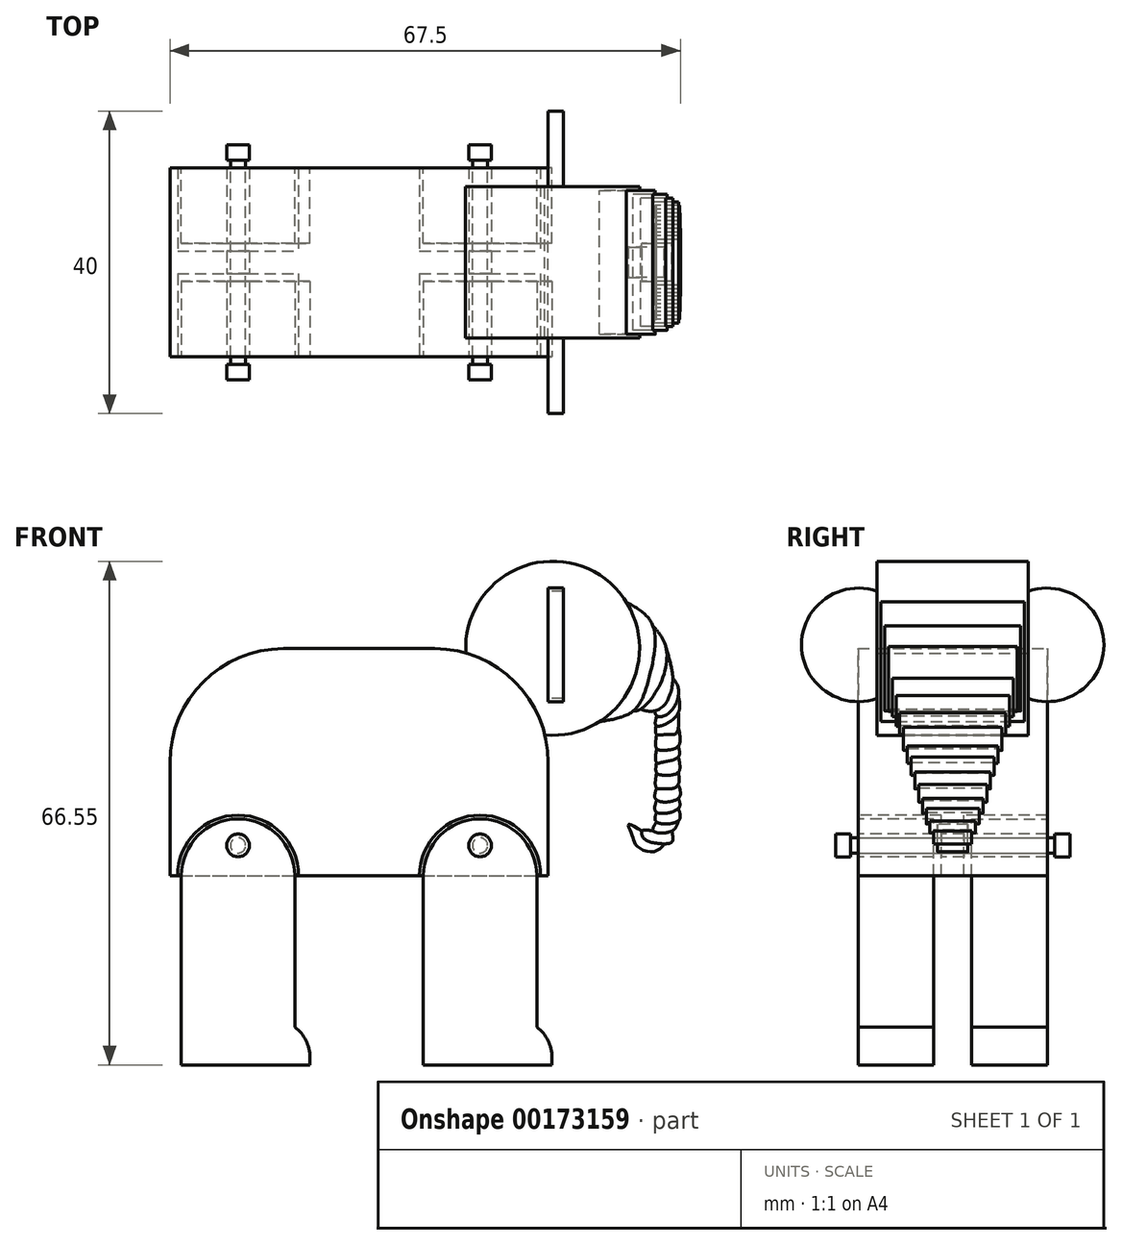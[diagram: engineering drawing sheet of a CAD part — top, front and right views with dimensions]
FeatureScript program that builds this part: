
annotation { "Feature Type Name" : "Feature", "Feature Type Description" : "" }
export const myFeature = defineFeature(function(context is Context, id is Id, definition is map)
    precondition{}
    {
        {
            var Q0;
            Q0=qCreatedBy(makeId("Front.planeOp"),FACE);
            var sketch = newSketch(context, id + "F0", { "sketchPlane" : qUnion([Q0])});
            skLineSegment(sketch, "E0.bottom", {"start": v(0, 0) * mm, "end": v(25, 0) * mm});
            skLineSegment(sketch, "E0.top", {"start": v(0, 30) * mm, "end": v(25, 30) * mm});
            skLineSegment(sketch, "E0.left", {"start": v(0, 0) * mm, "end": v(0, 30) * mm});
            skLineSegment(sketch, "E0.right", {"start": v(25, 0) * mm, "end": v(25, 30) * mm});
            skLineSegment(sketch, "E1.bottom", {"start": v(0, 0) * mm, "end": v(-25, 0) * mm});
            skLineSegment(sketch, "E1.top", {"start": v(0, 30) * mm, "end": v(-25, 30) * mm});
            skLineSegment(sketch, "E1.right", {"start": v(-25, 0) * mm, "end": v(-25, 30) * mm});
            skSolve(sketch);
        }
        {
            var Q0;
            Q0=makeQuery(id+"F0.imprint","IMPRINT",FACE,{"disambiguationData":[TD([[makeQuery(id+"F0.imprint","IMPRINT",EDGE,{"derivedFrom":sQuery(id+"F0.wireOp",EDGE,"E1.bottom")}),-1.0]])]});
            var Q1;
            Q1=makeQuery(id+"F0.imprint","IMPRINT",FACE,{"disambiguationData":[TD([[makeQuery(id+"F0.imprint","IMPRINT",EDGE,{"derivedFrom":sQuery(id+"F0.wireOp",EDGE,"E0.bottom")}),1.0]])]});
            extrude(context, id + "F1", {"entities" : qUnion([Q0, Q1]), "endBound" : BoundingType.SYMMETRIC, "depth" : 25 * mm});
        }
        {
            var Q0;
            Q0=makeQuery(id+"F1.opExtrude","SWEPT_EDGE",EDGE,{"disambiguationData":[OSD([sQuery(id+"F0.wireOp",EDGE,"E0.top"),sQuery(id+"F0.wireOp",EDGE,"E0.right")])]});
            var Q1;
            Q1=makeQuery(id+"F1.opExtrude","SWEPT_EDGE",EDGE,{"disambiguationData":[OSD([sQuery(id+"F0.wireOp",EDGE,"E1.top"),sQuery(id+"F0.wireOp",EDGE,"E1.right")])]});
            fillet(context, id + "F2", {"entities" : qUnion([Q0, Q1]), "radius" : 15 * mm, "tangentPropagation" : true, "allowEdgeOverflow" : false});
        }
        {
            var Q0;
            Q0=makeQuery(id+"F1.opExtrude","CAP_FACE",FACE,{"disambiguationData":[OSD([sQuery(id+"F0.wireOp",EDGE,"E0.bottom"),sQuery(id+"F0.wireOp",EDGE,"E0.top"),sQuery(id+"F0.wireOp",EDGE,"E0.right"),sQuery(id+"F0.wireOp",EDGE,"E1.bottom"),sQuery(id+"F0.wireOp",EDGE,"E1.top"),sQuery(id+"F0.wireOp",EDGE,"E1.right")])],"isStart":false});
            var sketch = newSketch(context, id + "F3", { "sketchPlane" : qUnion([Q0])});
            skCircle(sketch, "E2", {"center": v(-16, 0) * mm, "radius": 8 * mm});
            skCircle(sketch, "E3", {"center": v(16, 0) * mm, "radius": 8 * mm});
            skSolve(sketch);
        }
        {
            var Q0;
            Q0=sQuery(id+"F3.wireOp",VERTEX,"E2.center");
            var Q1;
            Q1=sQuery(id+"F3.wireOp",VERTEX,"E3.center");
            var Q2;
            Q2=makeQuery(id+"F1.opExtrude","SWEPT_BODY",BODY,{"disambiguationData":[OSD([sQuery(id+"F0.wireOp",EDGE,"E0.bottom"),sQuery(id+"F0.wireOp",EDGE,"E0.top"),sQuery(id+"F0.wireOp",EDGE,"E0.right"),sQuery(id+"F0.wireOp",EDGE,"E1.bottom"),sQuery(id+"F0.wireOp",EDGE,"E1.top"),sQuery(id+"F0.wireOp",EDGE,"E1.right")])]});
            hole(context, id + "F4", {"style" : HoleStyle.SIMPLE, "endStyle" : HoleEndStyle.THROUGH, "holeDiameter" : 16 * mm, "startFromSketch" : true, "locations" : qUnion([Q0, Q1]), "scope" : qUnion([Q2]), "isTappedThrough" : true});
        }
        {
            var Q0;
            Q0=qCreatedBy(makeId("Top.planeOp"),FACE);
            var sketch = newSketch(context, id + "F5", { "sketchPlane" : qUnion([Q0])});
            skLineSegment(sketch, "E4.bottom", {"start": v(-25, -1.5) * mm, "end": v(25, -1.5) * mm});
            skLineSegment(sketch, "E4.top", {"start": v(-25, 1.5) * mm, "end": v(25, 1.5) * mm});
            skLineSegment(sketch, "E4.left", {"start": v(-25, -1.5) * mm, "end": v(-25, 1.5) * mm});
            skLineSegment(sketch, "E4.right", {"start": v(25, -1.5) * mm, "end": v(25, 1.5) * mm});
            skSolve(sketch);
        }
        {
            var Q0;
            Q0=makeQuery(id+"F5.imprint","IMPRINT",FACE,{"disambiguationData":[TD([[makeQuery(id+"F5.imprint","IMPRINT",EDGE,{"derivedFrom":sQuery(id+"F5.wireOp",EDGE,"E4.bottom")}),1.0]])]});
            var Q1;
            Q1=makeQuery(id+"F1.opExtrude","SWEPT_BODY",BODY,{"disambiguationData":[OSD([sQuery(id+"F0.wireOp",EDGE,"E0.bottom"),sQuery(id+"F0.wireOp",EDGE,"E0.top"),sQuery(id+"F0.wireOp",EDGE,"E0.right"),sQuery(id+"F0.wireOp",EDGE,"E1.bottom"),sQuery(id+"F0.wireOp",EDGE,"E1.top"),sQuery(id+"F0.wireOp",EDGE,"E1.right")])]});
            extrude(context, id + "F6", {"entities" : qUnion([Q0]), "operationType" : NewBodyOperationType.ADD, "endBound" : BoundingType.UP_TO_BODY, "endBoundEntityBody" : qUnion([Q1]), "depth" : 25 * mm});
        }
        {
            var Q0;
            Q0=makeQuery(id+"F1.opExtrude","CAP_FACE",FACE,{"disambiguationData":[OSD([sQuery(id+"F0.wireOp",EDGE,"E0.bottom"),sQuery(id+"F0.wireOp",EDGE,"E0.top"),sQuery(id+"F0.wireOp",EDGE,"E0.right"),sQuery(id+"F0.wireOp",EDGE,"E1.bottom"),sQuery(id+"F0.wireOp",EDGE,"E1.top"),sQuery(id+"F0.wireOp",EDGE,"E1.right")])],"isStart":false});
            var sketch = newSketch(context, id + "F7", { "sketchPlane" : qUnion([Q0])});
            skLineSegment(sketch, "E5.top", {"start": v(-23.5, -25) * mm, "end": v(-8.5, -25) * mm});
            skLineSegment(sketch, "E5.left", {"start": v(-23.5, 0) * mm, "end": v(-23.5, -25) * mm});
            skLineSegment(sketch, "E5.right", {"start": v(-8.5, 0) * mm, "end": v(-8.5, -25) * mm});
            skArc(sketch, "E6", {"start": v(-8.5, 0) * mm, "mid": v(-16, 7.5) * mm, "end": v(-23.5, 0) * mm});
            skLineSegment(sketch, "E7", {"start": v(-23.5, 0) * mm, "end": v(-8.5, 0) * mm});
            skLineSegment(sketch, "E8.bottom", {"start": v(8.5, 0) * mm, "end": v(23.5, 0) * mm});
            skLineSegment(sketch, "E8.top", {"start": v(8.5, -25) * mm, "end": v(23.5, -25) * mm});
            skLineSegment(sketch, "E8.left", {"start": v(8.5, 0) * mm, "end": v(8.5, -25) * mm});
            skLineSegment(sketch, "E8.right", {"start": v(23.5, 0) * mm, "end": v(23.5, -25) * mm});
            skCircle(sketch, "E9", {"center": v(16, 0) * mm, "radius": 7.5 * mm});
            skLineSegment(sketch, "E10.bottom", {"start": v(-8.5, -25) * mm, "end": v(-6.5, -25) * mm});
            skLineSegment(sketch, "E10.top", {"start": v(-8.5, -20) * mm, "end": v(-6.5, -20) * mm});
            skLineSegment(sketch, "E10.left", {"start": v(-8.5, -25) * mm, "end": v(-8.5, -20) * mm});
            skLineSegment(sketch, "E10.right", {"start": v(-6.5, -25) * mm, "end": v(-6.5, -20) * mm});
            skLineSegment(sketch, "E11.bottom", {"start": v(23.5, -25) * mm, "end": v(25.5, -25) * mm});
            skLineSegment(sketch, "E11.top", {"start": v(23.5, -20) * mm, "end": v(25.5, -20) * mm});
            skLineSegment(sketch, "E11.left", {"start": v(23.5, -25) * mm, "end": v(23.5, -20) * mm});
            skLineSegment(sketch, "E11.right", {"start": v(25.5, -25) * mm, "end": v(25.5, -20) * mm});
            skSolve(sketch);
        }
        {
            var Q0;
            Q0=makeQuery(id+"F7.imprint","IMPRINT",FACE,{"disambiguationData":[TD([[makeQuery(id+"F7.imprint","IMPRINT",EDGE,{"derivedFrom":sQuery(id+"F7.wireOp",EDGE,"E6")}),1.0]])]});
            var Q1;
            Q1=makeQuery(id+"F7.imprint","IMPRINT",FACE,{"disambiguationData":[TD([[makeQuery(id+"F7.imprint","IMPRINT",EDGE,{"derivedFrom":sQuery(id+"F7.wireOp",EDGE,"E5.top")}),1.0]])]});
            var Q2;
            Q2=makeQuery(id+"F7.imprint","IMPRINT",FACE,{"disambiguationData":[TD([[makeQuery(id+"F7.imprint","IMPRINT",EDGE,{"derivedFrom":sQuery(id+"F7.wireOp",EDGE,"E8.top")}),1.0]])]});
            var Q3;
            {var subQ0=sQuery(id+"F7.wireOp",EDGE,"E8.bottom");Q3=makeQuery(id+"F7.imprint","IMPRINT",FACE,{"disambiguationData":[TD([[makeQuery(id+"F7.imprint","IMPRINT",EDGE,{"derivedFrom":subQ0}),-1.0]])]});}
            var Q4;
            {var subQ0=sQuery(id+"F7.wireOp",EDGE,"E8.bottom");Q4=makeQuery(id+"F7.imprint","IMPRINT",FACE,{"disambiguationData":[TD([[makeQuery(id+"F7.imprint","IMPRINT",EDGE,{"derivedFrom":subQ0}),1.0]])]});}
            var Q5;
            Q5=makeQuery(id+"F7.imprint","IMPRINT",FACE,{"disambiguationData":[TD([[makeQuery(id+"F7.imprint","IMPRINT",EDGE,{"derivedFrom":sQuery(id+"F7.wireOp",EDGE,"E10.bottom")}),1.0]])]});
            var Q6;
            Q6=makeQuery(id+"F7.imprint","IMPRINT",FACE,{"disambiguationData":[TD([[makeQuery(id+"F7.imprint","IMPRINT",EDGE,{"derivedFrom":sQuery(id+"F7.wireOp",EDGE,"E11.bottom")}),1.0]])]});
            var Q7;
            {var subQ0=sQuery(id+"F5.wireOp",EDGE,"E4.bottom");Q7=makeQuery(id+"F6.boolean.opBoolean","SPLIT",FACE,{"disambiguationData":[TD([makeQuery(id+"F4.hole-0.boolean.opBoolean","COPY",FACE,{"derivedFrom":makeQuery(id+"F4.hole-0.opRevolve","SWEPT_FACE",FACE,{"disambiguationData":[OSD([sQuery(id+"F4.hole-0.sketch.wireOp",EDGE,"core_line_2")])]})})])],"derivedFrom":makeQuery(id+"F6.opExtrude","SWEPT_FACE",FACE,{"disambiguationData":[OSD([subQ0])]})});}
            extrude(context, id + "F8", {"entities" : qUnion([Q0, Q1, Q2, Q3, Q4, Q5, Q6]), "oppositeDirection" : true, "endBoundEntityFace" : qUnion([Q7]), "depth" : 10 * mm});
        }
        {
            var Q0;
            Q0=makeQuery(id+"F8.opExtrude","SWEPT_EDGE",EDGE,{"disambiguationData":[OSD([sQuery(id+"F7.wireOp",EDGE,"E10.top"),sQuery(id+"F7.wireOp",EDGE,"E10.right")])]});
            var Q1;
            Q1=makeQuery(id+"F8.opExtrude","SWEPT_EDGE",EDGE,{"disambiguationData":[OSD([sQuery(id+"F7.wireOp",EDGE,"E11.top"),sQuery(id+"F7.wireOp",EDGE,"E11.right")])]});
            fillet(context, id + "F9", {"entities" : qUnion([Q0, Q1]), "radius" : 5 * mm, "tangentPropagation" : true, "allowEdgeOverflow" : false});
        }
        {
            var Q0;
            Q0=makeQuery(id+"F1.opExtrude","CAP_FACE",FACE,{"disambiguationData":[OSD([sQuery(id+"F0.wireOp",EDGE,"E0.bottom"),sQuery(id+"F0.wireOp",EDGE,"E0.top"),sQuery(id+"F0.wireOp",EDGE,"E0.right"),sQuery(id+"F0.wireOp",EDGE,"E1.bottom"),sQuery(id+"F0.wireOp",EDGE,"E1.top"),sQuery(id+"F0.wireOp",EDGE,"E1.right")])],"isStart":true});
            var sketch = newSketch(context, id + "F10", { "sketchPlane" : qUnion([Q0])});
            skLineSegment(sketch, "E12.bottom", {"start": v(-23.5, 0) * mm, "end": v(-8.5, 0) * mm});
            skLineSegment(sketch, "E12.top", {"start": v(-23.5, -25) * mm, "end": v(-8.5, -25) * mm});
            skLineSegment(sketch, "E12.left", {"start": v(-23.5, 0) * mm, "end": v(-23.5, -25) * mm});
            skLineSegment(sketch, "E12.right", {"start": v(-8.5, 0) * mm, "end": v(-8.5, -25) * mm});
            skCircle(sketch, "E13", {"center": v(-16, 0) * mm, "radius": 7.5 * mm});
            skLineSegment(sketch, "E14.bottom", {"start": v(-23.5, -25) * mm, "end": v(-25.5, -25) * mm});
            skLineSegment(sketch, "E14.top", {"start": v(-23.5, -20) * mm, "end": v(-25.5, -20) * mm});
            skLineSegment(sketch, "E14.left", {"start": v(-23.5, -25) * mm, "end": v(-23.5, -20) * mm});
            skLineSegment(sketch, "E14.right", {"start": v(-25.5, -25) * mm, "end": v(-25.5, -20) * mm});
            skLineSegment(sketch, "E15.bottom", {"start": v(8.5, 0) * mm, "end": v(23.5, 0) * mm});
            skLineSegment(sketch, "E15.top", {"start": v(8.5, -25) * mm, "end": v(23.5, -25) * mm});
            skLineSegment(sketch, "E15.left", {"start": v(8.5, 0) * mm, "end": v(8.5, -25) * mm});
            skLineSegment(sketch, "E15.right", {"start": v(23.5, 0) * mm, "end": v(23.5, -25) * mm});
            skCircle(sketch, "E16", {"center": v(16, 0) * mm, "radius": 7.5 * mm});
            skLineSegment(sketch, "E17.bottom", {"start": v(8.5, -25) * mm, "end": v(6.5, -25) * mm});
            skLineSegment(sketch, "E17.top", {"start": v(8.5, -20) * mm, "end": v(6.5, -20) * mm});
            skLineSegment(sketch, "E17.left", {"start": v(8.5, -25) * mm, "end": v(8.5, -20) * mm});
            skLineSegment(sketch, "E17.right", {"start": v(6.5, -25) * mm, "end": v(6.5, -20) * mm});
            skSolve(sketch);
        }
        {
            var Q0;
            {var subQ0=sQuery(id+"F10.wireOp",EDGE,"E12.bottom");Q0=makeQuery(id+"F10.imprint","IMPRINT",FACE,{"disambiguationData":[TD([[makeQuery(id+"F10.imprint","IMPRINT",EDGE,{"derivedFrom":subQ0}),-1.0]])]});}
            var Q1;
            {var subQ0=sQuery(id+"F10.wireOp",EDGE,"E12.bottom");Q1=makeQuery(id+"F10.imprint","IMPRINT",FACE,{"disambiguationData":[TD([[makeQuery(id+"F10.imprint","IMPRINT",EDGE,{"derivedFrom":subQ0}),1.0]])]});}
            var Q2;
            Q2=makeQuery(id+"F10.imprint","IMPRINT",FACE,{"disambiguationData":[TD([[makeQuery(id+"F10.imprint","IMPRINT",EDGE,{"derivedFrom":sQuery(id+"F10.wireOp",EDGE,"E12.top")}),1.0]])]});
            var Q3;
            Q3=makeQuery(id+"F10.imprint","IMPRINT",FACE,{"disambiguationData":[TD([[makeQuery(id+"F10.imprint","IMPRINT",EDGE,{"derivedFrom":sQuery(id+"F10.wireOp",EDGE,"E14.bottom")}),-1.0]])]});
            var Q4;
            {var subQ0=sQuery(id+"F10.wireOp",EDGE,"E15.bottom");Q4=makeQuery(id+"F10.imprint","IMPRINT",FACE,{"disambiguationData":[TD([[makeQuery(id+"F10.imprint","IMPRINT",EDGE,{"derivedFrom":subQ0}),-1.0]])]});}
            var Q5;
            {var subQ0=sQuery(id+"F10.wireOp",EDGE,"E15.bottom");Q5=makeQuery(id+"F10.imprint","IMPRINT",FACE,{"disambiguationData":[TD([[makeQuery(id+"F10.imprint","IMPRINT",EDGE,{"derivedFrom":subQ0}),1.0]])]});}
            var Q6;
            Q6=makeQuery(id+"F10.imprint","IMPRINT",FACE,{"disambiguationData":[TD([[makeQuery(id+"F10.imprint","IMPRINT",EDGE,{"derivedFrom":sQuery(id+"F10.wireOp",EDGE,"E15.top")}),1.0]])]});
            var Q7;
            Q7=makeQuery(id+"F10.imprint","IMPRINT",FACE,{"disambiguationData":[TD([[makeQuery(id+"F10.imprint","IMPRINT",EDGE,{"derivedFrom":sQuery(id+"F10.wireOp",EDGE,"E17.bottom")}),-1.0]])]});
            extrude(context, id + "F11", {"entities" : qUnion([Q0, Q1, Q2, Q3, Q4, Q5, Q6, Q7]), "oppositeDirection" : true, "depth" : 10 * mm});
        }
        {
            var Q0;
            Q0=makeQuery(id+"F11.opExtrude","SWEPT_EDGE",EDGE,{"disambiguationData":[OSD([sQuery(id+"F10.wireOp",EDGE,"E14.top"),sQuery(id+"F10.wireOp",EDGE,"E14.right")])]});
            var Q1;
            Q1=makeQuery(id+"F11.opExtrude","SWEPT_EDGE",EDGE,{"disambiguationData":[OSD([sQuery(id+"F10.wireOp",EDGE,"E17.top"),sQuery(id+"F10.wireOp",EDGE,"E17.right")])]});
            fillet(context, id + "F12", {"entities" : qUnion([Q0, Q1]), "radius" : 5 * mm, "tangentPropagation" : true, "allowEdgeOverflow" : false});
        }
        {
            var Q0;
            Q0=makeQuery(id+"F1.opExtrude","CAP_FACE",FACE,{"disambiguationData":[OSD([sQuery(id+"F0.wireOp",EDGE,"E0.bottom"),sQuery(id+"F0.wireOp",EDGE,"E0.top"),sQuery(id+"F0.wireOp",EDGE,"E0.right"),sQuery(id+"F0.wireOp",EDGE,"E1.bottom"),sQuery(id+"F0.wireOp",EDGE,"E1.top"),sQuery(id+"F0.wireOp",EDGE,"E1.right")])],"isStart":false});
            var sketch = newSketch(context, id + "F13", { "sketchPlane" : qUnion([Q0])});
            skCircle(sketch, "E18", {"center": v(-16, 4) * mm, "radius": 1.5 * mm});
            skCircle(sketch, "E19", {"center": v(16, 4) * mm, "radius": 1.5 * mm});
            skSolve(sketch);
        }
        {
            var Q0;
            Q0=sQuery(id+"F13.wireOp",VERTEX,"E18.center");
            var Q1;
            Q1=sQuery(id+"F13.wireOp",VERTEX,"E19.center");
            var Q2;
            Q2=makeQuery(id+"F8.opExtrude","SWEPT_BODY",BODY,{"disambiguationData":[OSD([sQuery(id+"F7.wireOp",EDGE,"E5.top"),sQuery(id+"F7.wireOp",EDGE,"E5.left"),sQuery(id+"F7.wireOp",EDGE,"E5.right"),sQuery(id+"F7.wireOp",EDGE,"E6"),sQuery(id+"F7.wireOp",EDGE,"E10.bottom"),sQuery(id+"F7.wireOp",EDGE,"E10.top"),sQuery(id+"F7.wireOp",EDGE,"E10.right")])]});
            var Q3;
            Q3=makeQuery(id+"F8.opExtrude","SWEPT_BODY",BODY,{"disambiguationData":[OSD([sQuery(id+"F7.wireOp",EDGE,"E8.top"),sQuery(id+"F7.wireOp",EDGE,"E8.left"),sQuery(id+"F7.wireOp",EDGE,"E8.right"),sQuery(id+"F7.wireOp",EDGE,"E9"),sQuery(id+"F7.wireOp",EDGE,"E11.bottom"),sQuery(id+"F7.wireOp",EDGE,"E11.top"),sQuery(id+"F7.wireOp",EDGE,"E11.right")])]});
            var Q4;
            Q4=makeQuery(id+"F1.opExtrude","SWEPT_BODY",BODY,{"disambiguationData":[OSD([sQuery(id+"F0.wireOp",EDGE,"E0.bottom"),sQuery(id+"F0.wireOp",EDGE,"E0.top"),sQuery(id+"F0.wireOp",EDGE,"E0.right"),sQuery(id+"F0.wireOp",EDGE,"E1.bottom"),sQuery(id+"F0.wireOp",EDGE,"E1.top"),sQuery(id+"F0.wireOp",EDGE,"E1.right")])]});
            hole(context, id + "F14", {"style" : HoleStyle.SIMPLE, "endStyle" : HoleEndStyle.BLIND, "holeDiameter" : 3 * mm, "holeDepth" : 30 * mm, "startFromSketch" : true, "locations" : qUnion([Q0, Q1]), "scope" : qUnion([Q2, Q3, Q4])});
        }
        {
            var Q0;
            Q0=makeQuery(id+"F11.opExtrude","CAP_FACE",FACE,{"disambiguationData":[OSD([sQuery(id+"F10.wireOp",EDGE,"E15.top"),sQuery(id+"F10.wireOp",EDGE,"E15.left"),sQuery(id+"F10.wireOp",EDGE,"E15.right"),sQuery(id+"F10.wireOp",EDGE,"E16"),sQuery(id+"F10.wireOp",EDGE,"E17.bottom"),sQuery(id+"F10.wireOp",EDGE,"E17.top"),sQuery(id+"F10.wireOp",EDGE,"E17.right")])],"isStart":false});
            var sketch = newSketch(context, id + "F15", { "sketchPlane" : qUnion([Q0])});
            skCircle(sketch, "E20", {"center": v(-16, 4) * mm, "radius": 1.5 * mm});
            skCircle(sketch, "E21", {"center": v(16, 4) * mm, "radius": 1.5 * mm});
            skSolve(sketch);
        }
        {
            var Q0;
            Q0=sQuery(id+"F15.wireOp",VERTEX,"E20.center");
            var Q1;
            Q1=sQuery(id+"F15.wireOp",VERTEX,"E21.center");
            var Q2;
            Q2=makeQuery(id+"F11.opExtrude","SWEPT_BODY",BODY,{"disambiguationData":[OSD([sQuery(id+"F10.wireOp",EDGE,"E15.top"),sQuery(id+"F10.wireOp",EDGE,"E15.left"),sQuery(id+"F10.wireOp",EDGE,"E15.right"),sQuery(id+"F10.wireOp",EDGE,"E16"),sQuery(id+"F10.wireOp",EDGE,"E17.bottom"),sQuery(id+"F10.wireOp",EDGE,"E17.top"),sQuery(id+"F10.wireOp",EDGE,"E17.right")])]});
            var Q3;
            Q3=makeQuery(id+"F11.opExtrude","SWEPT_BODY",BODY,{"disambiguationData":[OSD([sQuery(id+"F10.wireOp",EDGE,"E12.top"),sQuery(id+"F10.wireOp",EDGE,"E12.left"),sQuery(id+"F10.wireOp",EDGE,"E12.right"),sQuery(id+"F10.wireOp",EDGE,"E13"),sQuery(id+"F10.wireOp",EDGE,"E14.bottom"),sQuery(id+"F10.wireOp",EDGE,"E14.top"),sQuery(id+"F10.wireOp",EDGE,"E14.right")])]});
            hole(context, id + "F16", {"style" : HoleStyle.SIMPLE, "endStyle" : HoleEndStyle.THROUGH, "holeDiameter" : 3 * mm, "startFromSketch" : true, "locations" : qUnion([Q0, Q1]), "scope" : qUnion([Q2, Q3]), "isTappedThrough" : true});
        }
        {
            var Q0;
            Q0=qCreatedBy(makeId("Front.planeOp"),FACE);
            var sketch = newSketch(context, id + "F17", { "sketchPlane" : qUnion([Q0])});
            skCircle(sketch, "E22", {"center": v(-16, 4) * mm, "radius": 1 * mm});
            skCircle(sketch, "E23", {"center": v(16, 4) * mm, "radius": 1 * mm});
            skSolve(sketch);
        }
        {
            var Q0;
            Q0=makeQuery(id+"F17.imprint","IMPRINT",FACE,{"disambiguationData":[TD([[makeQuery(id+"F17.imprint","IMPRINT",EDGE,{"derivedFrom":sQuery(id+"F17.wireOp",EDGE,"E22")}),1.0]])]});
            var Q1;
            Q1=makeQuery(id+"F17.imprint","IMPRINT",FACE,{"disambiguationData":[TD([[makeQuery(id+"F17.imprint","IMPRINT",EDGE,{"derivedFrom":sQuery(id+"F17.wireOp",EDGE,"E23")}),1.0]])]});
            extrude(context, id + "F18", {"entities" : qUnion([Q0, Q1]), "endBound" : BoundingType.SYMMETRIC, "depth" : 27 * mm});
        }
        {
            var Q0;
            Q0=makeQuery(id+"F18.opExtrude","CAP_FACE",FACE,{"disambiguationData":[OSD([sQuery(id+"F17.wireOp",EDGE,"E22")])],"isStart":false});
            var sketch = newSketch(context, id + "F19", { "sketchPlane" : qUnion([Q0])});
            skCircle(sketch, "E24", {"center": v(-16, 4) * mm, "radius": 1.5 * mm});
            skCircle(sketch, "E25", {"center": v(16, 4) * mm, "radius": 1.5 * mm});
            skSolve(sketch);
        }
        {
            var Q0;
            Q0=makeQuery(id+"F19.imprint","IMPRINT",FACE,{"disambiguationData":[TD([[makeQuery(id+"F19.imprint","IMPRINT",EDGE,{"derivedFrom":sQuery(id+"F19.wireOp",EDGE,"E24")}),1.0]])]});
            var Q1;
            Q1=makeQuery(id+"F19.imprint","IMPRINT",FACE,{"disambiguationData":[TD([[makeQuery(id+"F19.imprint","IMPRINT",EDGE,{"derivedFrom":sQuery(id+"F19.wireOp",EDGE,"E25")}),1.0]])]});
            var Q2;
            Q2=makeQuery(id+"F19.imprint","IMPRINT",FACE,{"disambiguationData":[TD([[makeQuery(id+"F19.imprint","IMPRINT",EDGE,{"derivedFrom":makeQuery(id+"F18.opExtrude","CAP_EDGE",EDGE,{"disambiguationData":[OSD([sQuery(id+"F17.wireOp",EDGE,"E22")])],"isStart":false})}),1.0]])]});
            extrude(context, id + "F20", {"entities" : qUnion([Q0, Q1, Q2]), "operationType" : NewBodyOperationType.ADD, "depth" : 2 * mm});
        }
        {
            var Q0;
            Q0=makeQuery(id+"F18.opExtrude","CAP_FACE",FACE,{"disambiguationData":[OSD([sQuery(id+"F17.wireOp",EDGE,"E23")])],"isStart":true});
            var sketch = newSketch(context, id + "F21", { "sketchPlane" : qUnion([Q0])});
            skCircle(sketch, "E26", {"center": v(-16, 4) * mm, "radius": 1.5 * mm});
            skCircle(sketch, "E27", {"center": v(16, 4) * mm, "radius": 1.5 * mm});
            skSolve(sketch);
        }
        {
            var Q0;
            Q0=makeQuery(id+"F21.imprint","IMPRINT",FACE,{"disambiguationData":[TD([[makeQuery(id+"F21.imprint","IMPRINT",EDGE,{"derivedFrom":makeQuery(id+"F18.opExtrude","CAP_EDGE",EDGE,{"disambiguationData":[OSD([sQuery(id+"F17.wireOp",EDGE,"E23")])],"isStart":true})}),-1.0]])]});
            var Q1;
            Q1=makeQuery(id+"F21.imprint","IMPRINT",FACE,{"disambiguationData":[TD([[makeQuery(id+"F21.imprint","IMPRINT",EDGE,{"derivedFrom":sQuery(id+"F21.wireOp",EDGE,"E26")}),1.0]])]});
            var Q2;
            Q2=makeQuery(id+"F21.imprint","IMPRINT",FACE,{"disambiguationData":[TD([[makeQuery(id+"F21.imprint","IMPRINT",EDGE,{"derivedFrom":sQuery(id+"F21.wireOp",EDGE,"E27")}),1.0]])]});
            extrude(context, id + "F22", {"entities" : qUnion([Q0, Q1, Q2]), "depth" : 2 * mm});
        }
        {
            var Q0;
            Q0=qCreatedBy(makeId("Front.planeOp"),FACE);
            var sketch = newSketch(context, id + "F23", { "sketchPlane" : qUnion([Q0])});
            skCircle(sketch, "E28", {"center": v(25.6, 30.05) * mm, "radius": 11.5 * mm});
            skSolve(sketch);
        }
        {
            var Q0;
            Q0=makeQuery(id+"F23.imprint","IMPRINT",FACE,{"disambiguationData":[TD([[makeQuery(id+"F23.imprint","IMPRINT",EDGE,{"derivedFrom":sQuery(id+"F23.wireOp",EDGE,"E28")}),1.0]])]});
            extrude(context, id + "F24", {"entities" : qUnion([Q0]), "operationType" : NewBodyOperationType.ADD, "endBound" : BoundingType.SYMMETRIC, "depth" : 20 * mm});
        }
        {
            var Q0;
            Q0=makeQuery(id+"F1.opExtrude","SWEPT_FACE",FACE,{"disambiguationData":[OSD([sQuery(id+"F0.wireOp",EDGE,"E0.right")])]});
            var sketch = newSketch(context, id + "F25", { "sketchPlane" : qUnion([Q0])});
            skCircle(sketch, "E29", {"center": v(12.5, 30.5) * mm, "radius": 7.5 * mm});
            skCircle(sketch, "E30", {"center": v(-12.5, 30.5) * mm, "radius": 7.5 * mm});
            skSolve(sketch);
        }
        {
            var Q0;
            Q0=makeQuery(id+"F25.imprint","IMPRINT",FACE,{"disambiguationData":[TD([[makeQuery(id+"F25.imprint","IMPRINT",EDGE,{"derivedFrom":sQuery(id+"F25.wireOp",EDGE,"E30")}),1.0]])]});
            var Q1;
            Q1=makeQuery(id+"F25.imprint","IMPRINT",FACE,{"disambiguationData":[TD([[makeQuery(id+"F25.imprint","IMPRINT",EDGE,{"derivedFrom":sQuery(id+"F25.wireOp",EDGE,"E29")}),1.0]])]});
            extrude(context, id + "F26", {"entities" : qUnion([Q0, Q1]), "operationType" : NewBodyOperationType.ADD, "depth" : 2 * mm});
        }
        {
            var Q0;
            Q0=qCreatedBy(makeId("Front.planeOp"),FACE);
            var sketch = newSketch(context, id + "F27", { "sketchPlane" : qUnion([Q0])});
            skFitSpline(sketch, "E31", {"points": [v(40.56, 30.28) * mm, v(41.43, 26.75) * mm, v(41.34, 24.75) * mm, v(40.38, 22.58) * mm, v(39.1, 21.78) * mm, v(37.98, 21.78) * mm, v(37.22, 22.01) * mm], "startDerivative": vector(4.65, -16.05) * mm, "endDerivative": vector(-6.4, 2.73) * mm});
            skFitSpline(sketch, "E32", {"points": [v(41.48, 26.11) * mm, v(42.23, 24.75) * mm, v(41.83, 22.58) * mm, v(40.38, 21.14) * mm, v(39.34, 21.14) * mm, v(39.1, 21.78) * mm], "startDerivative": vector(4.62, -5.94) * mm, "endDerivative": vector(-0.74, 5.49) * mm});
            skFitSpline(sketch, "E33", {"points": [v(42.23, 23.78) * mm, v(42.23, 21.54) * mm, v(40.3, 19.94) * mm, v(39.26, 19.86) * mm, v(39.34, 21.14) * mm], "startDerivative": vector(1.66, -8.22) * mm, "endDerivative": vector(1.8, 7.43) * mm});
            skFitSpline(sketch, "E34", {"points": [v(42.23, 21.54) * mm, v(42.23, 19.62) * mm, v(41.8, 18.73) * mm, v(40.38, 18.65) * mm, v(39.34, 18.65) * mm, v(39.26, 19.86) * mm], "startDerivative": vector(0.43, -8.38) * mm, "endDerivative": vector(0.93, 8) * mm});
            skFitSpline(sketch, "E35", {"points": [v(42.23, 19.62) * mm, v(42.23, 17.13) * mm, v(40.38, 16.57) * mm, v(39.34, 16.8) * mm, v(39.34, 18.65) * mm], "startDerivative": vector(2.08, -10.06) * mm, "endDerivative": vector(1.38, 8.95) * mm});
            skFitSpline(sketch, "E36", {"points": [v(42.23, 17.13) * mm, v(42.23, 15.69) * mm, v(40.38, 15.04) * mm, v(39.34, 14.96) * mm, v(39.34, 16.8) * mm], "startDerivative": vector(1.68, -6.89) * mm, "endDerivative": vector(1.3, 8.85) * mm});
            skFitSpline(sketch, "E37", {"points": [v(42.23, 15.69) * mm, v(42.23, 13.68) * mm, v(40.38, 13.28) * mm, v(39.34, 13.6) * mm, v(39.34, 14.96) * mm], "startDerivative": vector(1.88, -8.46) * mm, "endDerivative": vector(1.18, 6.94) * mm});
            skFitSpline(sketch, "E38", {"points": [v(42.23, 13.68) * mm, v(42.23, 12.08) * mm, v(41.48, 11.52) * mm, v(40.38, 11.52) * mm, v(39.34, 11.6) * mm, v(39.34, 13.6) * mm], "startDerivative": vector(1.22, -8.14) * mm, "endDerivative": vector(1.76, 10.47) * mm});
            skFitSpline(sketch, "E39", {"points": [v(42.23, 12.08) * mm, v(42.23, 10.23) * mm, v(39.34, 10) * mm, v(39.34, 11.6) * mm], "startDerivative": vector(2.28, -6.73) * mm, "endDerivative": vector(2.17, 6.55) * mm});
            skFitSpline(sketch, "E40", {"points": [v(42.23, 10.23) * mm, v(42.23, 8.87) * mm, v(39.34, 8.39) * mm, v(39.34, 10) * mm], "startDerivative": vector(2, -5.25) * mm, "endDerivative": vector(2.11, 6.49) * mm});
            skFitSpline(sketch, "E41", {"points": [v(42.23, 8.87) * mm, v(42.23, 7.26) * mm, v(39.34, 7.1) * mm, v(39.34, 8.39) * mm], "startDerivative": vector(2.11, -5.96) * mm, "endDerivative": vector(1.96, 5.44) * mm});
            skFitSpline(sketch, "E42", {"points": [v(42.23, 7.26) * mm, v(41.34, 5.9) * mm, v(38.94, 5.9) * mm, v(39.34, 7.1) * mm], "startDerivative": vector(-1.37, -4.96) * mm, "endDerivative": vector(3.34, 4.92) * mm});
            skFitSpline(sketch, "E43", {"points": [v(41.34, 5.9) * mm, v(41.34, 4.46) * mm, v(39.34, 4.3) * mm, v(37.66, 4.94) * mm, v(37.41, 5.9) * mm, v(38.94, 5.9) * mm], "startDerivative": vector(2.15, -8.95) * mm, "endDerivative": vector(9.95, -1.92) * mm});
            skFitSpline(sketch, "E44", {"points": [v(40.38, 4.2) * mm, v(38.94, 3.17) * mm, v(36.85, 3.82) * mm, v(36.3, 4.78) * mm, v(35.9, 5.9) * mm, v(35.65, 6.78) * mm, v(37.41, 5.9) * mm], "startDerivative": vector(-6.83, -7.7) * mm, "endDerivative": vector(12.58, -8.08) * mm});
            skFitSpline(sketch, "E45", {"points": [v(35.27, 36.2) * mm, v(38.85, 33.02) * mm, v(38.31, 26.02) * mm, v(36.23, 21.75) * mm, v(31.5, 20.33) * mm], "startDerivative": vector(18.96, -10.55) * mm, "endDerivative": vector(-22.43, -3.25) * mm});
            skFitSpline(sketch, "E46", {"points": [v(31.5, 20.33) * mm, v(33.93, 22.48) * mm, v(35.7, 25.06) * mm, v(36.73, 28.02) * mm, v(36.73, 31.55) * mm, v(36.12, 34.05) * mm, v(35.27, 36.2) * mm], "startDerivative": vector(14.67, 11.75) * mm, "endDerivative": vector(-6.05, 14.51) * mm});
            skFitSpline(sketch, "E47", {"points": [v(38.85, 33.02) * mm, v(40.56, 30.28) * mm, v(39.85, 25.4) * mm, v(37.22, 22.01) * mm, v(36.23, 21.75) * mm], "startDerivative": vector(8.42, -9.6) * mm, "endDerivative": vector(-6.37, -0.33) * mm});
            skSolve(sketch);
        }
        {
            var Q0;
            {var subQ0=sQuery(id+"F27.wireOp",EDGE,"E46");Q0=makeQuery(id+"F27.imprint","IMPRINT",FACE,{"disambiguationData":[TD([[makeQuery(id+"F27.imprint","IMPRINT",EDGE,{"derivedFrom":subQ0}),-1.0]])]});}
            extrude(context, id + "F28", {"entities" : qUnion([Q0]), "operationType" : NewBodyOperationType.ADD, "endBound" : BoundingType.SYMMETRIC, "depth" : 19 * mm});
        }
        {
            var Q0;
            {var subQ0=sQuery(id+"F27.wireOp",EDGE,"E47");var subQ1=sQuery(id+"F27.wireOp",EDGE,"E45");var subQ2=makeQuery(id+"F27.imprint","INTERSECT",VERTEX,{"disambiguationData":[OD(0.0)],"derivedFrom":[subQ1,subQ0]});Q0=makeQuery(id+"F27.imprint","IMPRINT",FACE,{"disambiguationData":[TD([[makeQuery(id+"F27.imprint","IMPRINT",EDGE,{"disambiguationData":[TD([[subQ2,-1.0]])],"derivedFrom":subQ1}),1.0]])]});}
            extrude(context, id + "F29", {"entities" : qUnion([Q0]), "operationType" : NewBodyOperationType.ADD, "endBound" : BoundingType.SYMMETRIC, "depth" : 18 * mm});
        }
        {
            var Q0;
            {var subQ0=sQuery(id+"F27.wireOp",EDGE,"E47");var subQ1=sQuery(id+"F27.wireOp",EDGE,"E31");var subQ2=makeQuery(id+"F27.imprint","INTERSECT",VERTEX,{"disambiguationData":[OD(0.0)],"derivedFrom":[subQ1,subQ0]});Q0=makeQuery(id+"F27.imprint","IMPRINT",FACE,{"disambiguationData":[TD([[makeQuery(id+"F27.imprint","IMPRINT",EDGE,{"disambiguationData":[TD([[subQ2,-1.0]])],"derivedFrom":subQ1}),-1.0]])]});}
            extrude(context, id + "F30", {"entities" : qUnion([Q0]), "operationType" : NewBodyOperationType.ADD, "endBound" : BoundingType.SYMMETRIC, "depth" : 17 * mm});
        }
        {
            var Q0;
            {var subQ0=sQuery(id+"F27.wireOp",EDGE,"E32");var subQ1=sQuery(id+"F27.wireOp",EDGE,"E31");var subQ2=makeQuery(id+"F27.imprint","INTERSECT",VERTEX,{"disambiguationData":[OD(0.0)],"derivedFrom":[subQ1,subQ0]});Q0=makeQuery(id+"F27.imprint","IMPRINT",FACE,{"disambiguationData":[TD([[makeQuery(id+"F27.imprint","IMPRINT",EDGE,{"disambiguationData":[TD([[subQ2,-1.0]])],"derivedFrom":subQ1}),1.0]])]});}
            extrude(context, id + "F31", {"entities" : qUnion([Q0]), "operationType" : NewBodyOperationType.ADD, "endBound" : BoundingType.SYMMETRIC, "depth" : 16 * mm});
        }
        {
            var Q0;
            {var subQ0=sQuery(id+"F27.wireOp",EDGE,"E33");var subQ1=sQuery(id+"F27.wireOp",EDGE,"E32");var subQ2=makeQuery(id+"F27.imprint","INTERSECT",VERTEX,{"disambiguationData":[OD(0.0)],"derivedFrom":[subQ1,subQ0]});Q0=makeQuery(id+"F27.imprint","IMPRINT",FACE,{"disambiguationData":[TD([[makeQuery(id+"F27.imprint","IMPRINT",EDGE,{"disambiguationData":[TD([[subQ2,-1.0]])],"derivedFrom":subQ1}),1.0]])]});}
            extrude(context, id + "F32", {"entities" : qUnion([Q0]), "operationType" : NewBodyOperationType.ADD, "endBound" : BoundingType.SYMMETRIC, "depth" : 15 * mm});
        }
        {
            var Q0;
            {var subQ0=sQuery(id+"F27.wireOp",EDGE,"E34");var subQ1=sQuery(id+"F27.wireOp",EDGE,"E33");var subQ2=makeQuery(id+"F27.imprint","INTERSECT",VERTEX,{"disambiguationData":[OD(0.0)],"derivedFrom":[subQ1,subQ0]});Q0=makeQuery(id+"F27.imprint","IMPRINT",FACE,{"disambiguationData":[TD([[makeQuery(id+"F27.imprint","IMPRINT",EDGE,{"disambiguationData":[TD([[subQ2,-1.0]])],"derivedFrom":subQ1}),1.0]])]});}
            extrude(context, id + "F33", {"entities" : qUnion([Q0]), "operationType" : NewBodyOperationType.ADD, "endBound" : BoundingType.SYMMETRIC, "depth" : 14 * mm});
        }
        {
            var Q0;
            {var subQ0=sQuery(id+"F27.wireOp",EDGE,"E35");var subQ1=sQuery(id+"F27.wireOp",EDGE,"E34");var subQ2=makeQuery(id+"F27.imprint","INTERSECT",VERTEX,{"disambiguationData":[OD(0.0)],"derivedFrom":[subQ1,subQ0]});Q0=makeQuery(id+"F27.imprint","IMPRINT",FACE,{"disambiguationData":[TD([[makeQuery(id+"F27.imprint","IMPRINT",EDGE,{"disambiguationData":[TD([[subQ2,-1.0]])],"derivedFrom":subQ1}),1.0]])]});}
            extrude(context, id + "F34", {"entities" : qUnion([Q0]), "operationType" : NewBodyOperationType.ADD, "endBound" : BoundingType.SYMMETRIC, "depth" : 13 * mm});
        }
        {
            var Q0;
            {var subQ0=sQuery(id+"F27.wireOp",EDGE,"E36");var subQ1=sQuery(id+"F27.wireOp",EDGE,"E35");var subQ2=makeQuery(id+"F27.imprint","INTERSECT",VERTEX,{"disambiguationData":[OD(0.0)],"derivedFrom":[subQ1,subQ0]});Q0=makeQuery(id+"F27.imprint","IMPRINT",FACE,{"disambiguationData":[TD([[makeQuery(id+"F27.imprint","IMPRINT",EDGE,{"disambiguationData":[TD([[subQ2,-1.0]])],"derivedFrom":subQ1}),1.0]])]});}
            extrude(context, id + "F35", {"entities" : qUnion([Q0]), "operationType" : NewBodyOperationType.ADD, "endBound" : BoundingType.SYMMETRIC, "depth" : 12 * mm});
        }
        {
            var Q0;
            {var subQ0=sQuery(id+"F27.wireOp",EDGE,"E37");var subQ1=sQuery(id+"F27.wireOp",EDGE,"E36");var subQ2=makeQuery(id+"F27.imprint","INTERSECT",VERTEX,{"disambiguationData":[OD(0.0)],"derivedFrom":[subQ1,subQ0]});Q0=makeQuery(id+"F27.imprint","IMPRINT",FACE,{"disambiguationData":[TD([[makeQuery(id+"F27.imprint","IMPRINT",EDGE,{"disambiguationData":[TD([[subQ2,-1.0]])],"derivedFrom":subQ1}),1.0]])]});}
            extrude(context, id + "F36", {"entities" : qUnion([Q0]), "operationType" : NewBodyOperationType.ADD, "endBound" : BoundingType.SYMMETRIC, "depth" : 11 * mm});
        }
        {
            var Q0;
            {var subQ0=sQuery(id+"F27.wireOp",EDGE,"E38");var subQ1=sQuery(id+"F27.wireOp",EDGE,"E37");var subQ2=makeQuery(id+"F27.imprint","INTERSECT",VERTEX,{"disambiguationData":[OD(0.0)],"derivedFrom":[subQ1,subQ0]});Q0=makeQuery(id+"F27.imprint","IMPRINT",FACE,{"disambiguationData":[TD([[makeQuery(id+"F27.imprint","IMPRINT",EDGE,{"disambiguationData":[TD([[subQ2,-1.0]])],"derivedFrom":subQ1}),1.0]])]});}
            extrude(context, id + "F37", {"entities" : qUnion([Q0]), "operationType" : NewBodyOperationType.ADD, "endBound" : BoundingType.SYMMETRIC, "depth" : 10 * mm});
        }
        {
            var Q0;
            {var subQ0=sQuery(id+"F27.wireOp",EDGE,"E39");var subQ1=sQuery(id+"F27.wireOp",EDGE,"E38");var subQ2=makeQuery(id+"F27.imprint","INTERSECT",VERTEX,{"disambiguationData":[OD(0.0)],"derivedFrom":[subQ1,subQ0]});Q0=makeQuery(id+"F27.imprint","IMPRINT",FACE,{"disambiguationData":[TD([[makeQuery(id+"F27.imprint","IMPRINT",EDGE,{"disambiguationData":[TD([[subQ2,-1.0]])],"derivedFrom":subQ1}),1.0]])]});}
            extrude(context, id + "F38", {"entities" : qUnion([Q0]), "operationType" : NewBodyOperationType.ADD, "endBound" : BoundingType.SYMMETRIC, "depth" : 9 * mm});
        }
        {
            var Q0;
            {var subQ0=sQuery(id+"F27.wireOp",EDGE,"E40");var subQ1=sQuery(id+"F27.wireOp",EDGE,"E39");var subQ2=makeQuery(id+"F27.imprint","INTERSECT",VERTEX,{"disambiguationData":[OD(0.0)],"derivedFrom":[subQ1,subQ0]});Q0=makeQuery(id+"F27.imprint","IMPRINT",FACE,{"disambiguationData":[TD([[makeQuery(id+"F27.imprint","IMPRINT",EDGE,{"disambiguationData":[TD([[subQ2,-1.0]])],"derivedFrom":subQ1}),1.0]])]});}
            extrude(context, id + "F39", {"entities" : qUnion([Q0]), "operationType" : NewBodyOperationType.ADD, "endBound" : BoundingType.SYMMETRIC, "depth" : 8 * mm});
        }
        {
            var Q0;
            {var subQ0=sQuery(id+"F27.wireOp",EDGE,"E41");var subQ1=sQuery(id+"F27.wireOp",EDGE,"E40");var subQ2=makeQuery(id+"F27.imprint","INTERSECT",VERTEX,{"disambiguationData":[OD(0.0)],"derivedFrom":[subQ1,subQ0]});Q0=makeQuery(id+"F27.imprint","IMPRINT",FACE,{"disambiguationData":[TD([[makeQuery(id+"F27.imprint","IMPRINT",EDGE,{"disambiguationData":[TD([[subQ2,-1.0]])],"derivedFrom":subQ1}),1.0]])]});}
            extrude(context, id + "F40", {"entities" : qUnion([Q0]), "operationType" : NewBodyOperationType.ADD, "endBound" : BoundingType.SYMMETRIC, "depth" : 7 * mm});
        }
        {
            var Q0;
            {var subQ0=sQuery(id+"F27.wireOp",EDGE,"E42");var subQ1=sQuery(id+"F27.wireOp",EDGE,"E41");var subQ2=makeQuery(id+"F27.imprint","INTERSECT",VERTEX,{"disambiguationData":[OD(0.0)],"derivedFrom":[subQ1,subQ0]});Q0=makeQuery(id+"F27.imprint","IMPRINT",FACE,{"disambiguationData":[TD([[makeQuery(id+"F27.imprint","IMPRINT",EDGE,{"disambiguationData":[TD([[subQ2,-1.0]])],"derivedFrom":subQ1}),1.0]])]});}
            extrude(context, id + "F41", {"entities" : qUnion([Q0]), "operationType" : NewBodyOperationType.ADD, "endBound" : BoundingType.SYMMETRIC, "depth" : 6 * mm});
        }
        {
            var Q0;
            {var subQ0=sQuery(id+"F27.wireOp",EDGE,"E43");var subQ1=sQuery(id+"F27.wireOp",EDGE,"E42");var subQ2=makeQuery(id+"F27.imprint","INTERSECT",VERTEX,{"disambiguationData":[OD(0.0)],"derivedFrom":[subQ1,subQ0]});Q0=makeQuery(id+"F27.imprint","IMPRINT",FACE,{"disambiguationData":[TD([[makeQuery(id+"F27.imprint","IMPRINT",EDGE,{"disambiguationData":[TD([[subQ2,-1.0]])],"derivedFrom":subQ1}),1.0]])]});}
            extrude(context, id + "F42", {"entities" : qUnion([Q0]), "operationType" : NewBodyOperationType.ADD, "endBound" : BoundingType.SYMMETRIC, "depth" : 5 * mm});
        }
        {
            var Q0;
            {var subQ0=sQuery(id+"F27.wireOp",EDGE,"E44");Q0=makeQuery(id+"F27.imprint","IMPRINT",FACE,{"disambiguationData":[TD([[makeQuery(id+"F27.imprint","IMPRINT",EDGE,{"derivedFrom":subQ0}),-1.0]])]});}
            extrude(context, id + "F43", {"entities" : qUnion([Q0]), "operationType" : NewBodyOperationType.ADD, "endBound" : BoundingType.SYMMETRIC, "depth" : 4 * mm});
        }
    });
